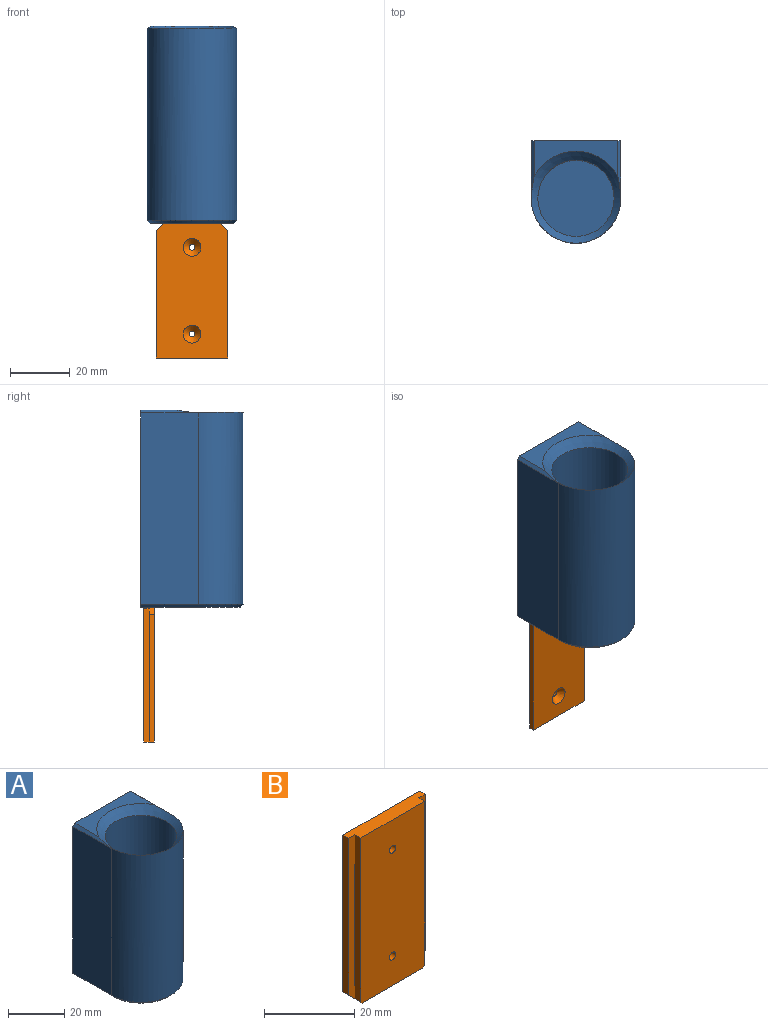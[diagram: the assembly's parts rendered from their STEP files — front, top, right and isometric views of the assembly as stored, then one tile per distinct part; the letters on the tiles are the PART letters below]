
ASSEMBLY  parts=2 mates=1
PART A: 22 faces, bbox 31.6x35.2x66.1 mm
  f0: plane 66x30mm, normal (0,1,0), area 958mm2, adj f1,f2,f4,f5,f8,f14,f15,f17
  f1: plane 33.29x28mm, normal (0,0,-1), area 744.8mm2, adj f0,f8,f9,f10,f11,f12,f13,f14
  f2: plane 64x19.29mm, normal (-1,0,0), area 1234.7mm2, adj f0,f3,f19,f21
  f3: cylinder r=15mm len=64.25mm, axis (0,0,-1), area 3027mm2, adj f2,f4,f16,f18,f20,f21
  f4: plane 64x19.29mm, normal (1,0,0), area 1234.7mm2, adj f0,f3,f17,f20
  f5: plane 28x12.08mm, normal (0,0,1), area 167.5mm2, adj f0,f16,f20,f21
  f6: cylinder r=12.75mm len=60.5mm, axis (0,0,1), area 4846.7mm2, adj f7,f16
  f7: plane 25.5x25.5mm, normal (0,0,1), area 510.7mm2, adj f6
  f8: plane 50x2.3mm, normal (-1,0,0), area 115mm2, adj f0,f1,f9,f15
  f9: plane 50x2.05mm, normal (0,-1,0), area 102.5mm2, adj f1,f8,f10,f15
  f10: plane 50x2.3mm, normal (-1,0,0), area 115mm2, adj f1,f9,f11,f15
  f11: plane 50x24.5mm, normal (0,1,0), area 1225mm2, adj f1,f10,f12,f15
  f12: plane 50x2.3mm, normal (1,0,0), area 115mm2, adj f1,f11,f13,f15
  f13: plane 50x2.05mm, normal (0,-1,0), area 102.5mm2, adj f1,f12,f14,f15
  f14: plane 50x2.3mm, normal (1,0,0), area 115mm2, adj f0,f1,f13,f15
  f15: plane 24.5x4.6mm, normal (0,0,-1), area 103.3mm2, adj f0,f8,f9,f10,f11,f12,f13,f14
  f16: cone r=12.75mm half-angle=45deg, axis (0,0,1), area 315.9mm2, adj f3,f5,f6,f20,f21
  f17: plane 19.29x1mm, normal (0.71,0,-0.71), area 27.3mm2, adj f0,f1,f4,f18
  f18: cone r=15mm half-angle=45deg, axis (0,0,1), area 64.4mm2, adj f1,f3,f17,f19
  f19: plane 19.29x1mm, normal (-0.71,0,-0.71), area 27.3mm2, adj f0,f1,f2,f18
  f20: plane 22.14x1.12mm, normal (0.71,0,0.71), area 21.7mm2, adj f0,f3,f4,f5,f16
  f21: plane 22.14x1.12mm, normal (-0.71,0,0.71), area 21.7mm2, adj f0,f2,f3,f5,f16
PART B: 16 faces, bbox 24x3.6x45 mm
  f0: plane 44.5x2mm, normal (0,-1,0), area 87mm2, adj f1,f7,f8,f11
  f1: plane 44.5x1.8mm, normal (-1,0,0), area 80.1mm2, adj f0,f2,f8,f11
  f2: plane 45x20mm, normal (0,-1,0), area 893.5mm2, adj f1,f3,f8,f9,f10,f11,f12,f14
  f3: plane 44.5x1.8mm, normal (1,0,0), area 80.1mm2, adj f2,f4,f8,f10
  f4: plane 44.5x2mm, normal (0,-1,0), area 87mm2, adj f3,f5,f8,f10
  f5: plane 42.5x1.8mm, normal (1,0,0), area 76.5mm2, adj f4,f6,f8,f10
  f6: plane 45x24mm, normal (0,1,0), area 1017.2mm2, adj f5,f7,f8,f9,f10,f11,f13,f15
  f7: plane 42.5x1.8mm, normal (-1,0,0), area 76.5mm2, adj f0,f6,f8,f11
  f8: plane 24x3.6mm, normal (0,0,1), area 79.2mm2, adj f0,f1,f2,f3,f4,f5,f6,f7
  f9: plane 19x3.6mm, normal (0,0,-1), area 68.4mm2, adj f2,f6,f10,f11
  f10: plane 3.6x2.5mm, normal (0.71,0,-0.71), area 7.6mm2, adj f2,f3,f4,f5,f6,f9
  f11: plane 3.6x2.5mm, normal (-0.71,0,-0.71), area 7.6mm2, adj f0,f1,f2,f6,f7,f9
  f12: cylinder r=1mm len=2mm, axis (0,1,0), area 10.1mm2, adj f2,f13
  f13: cone r=1mm half-angle=45deg, axis (0,1,0), area 35.5mm2, adj f6,f12
  f14: cylinder r=1mm len=2mm, axis (0,1,0), area 10.1mm2, adj f2,f15
  f15: cone r=1mm half-angle=45deg, axis (0,1,0), area 35.5mm2, adj f6,f14
PLACE A t=(-24.77,0.31,-9.31)mm
PLACE B rot(axis=(1,0,0),180deg) t=(-24.77,18.41,-9.31)mm
MATE slider B.f9 <-> A.f1  axis (0,0,1) through (-24.77,15,-9.31)mm
